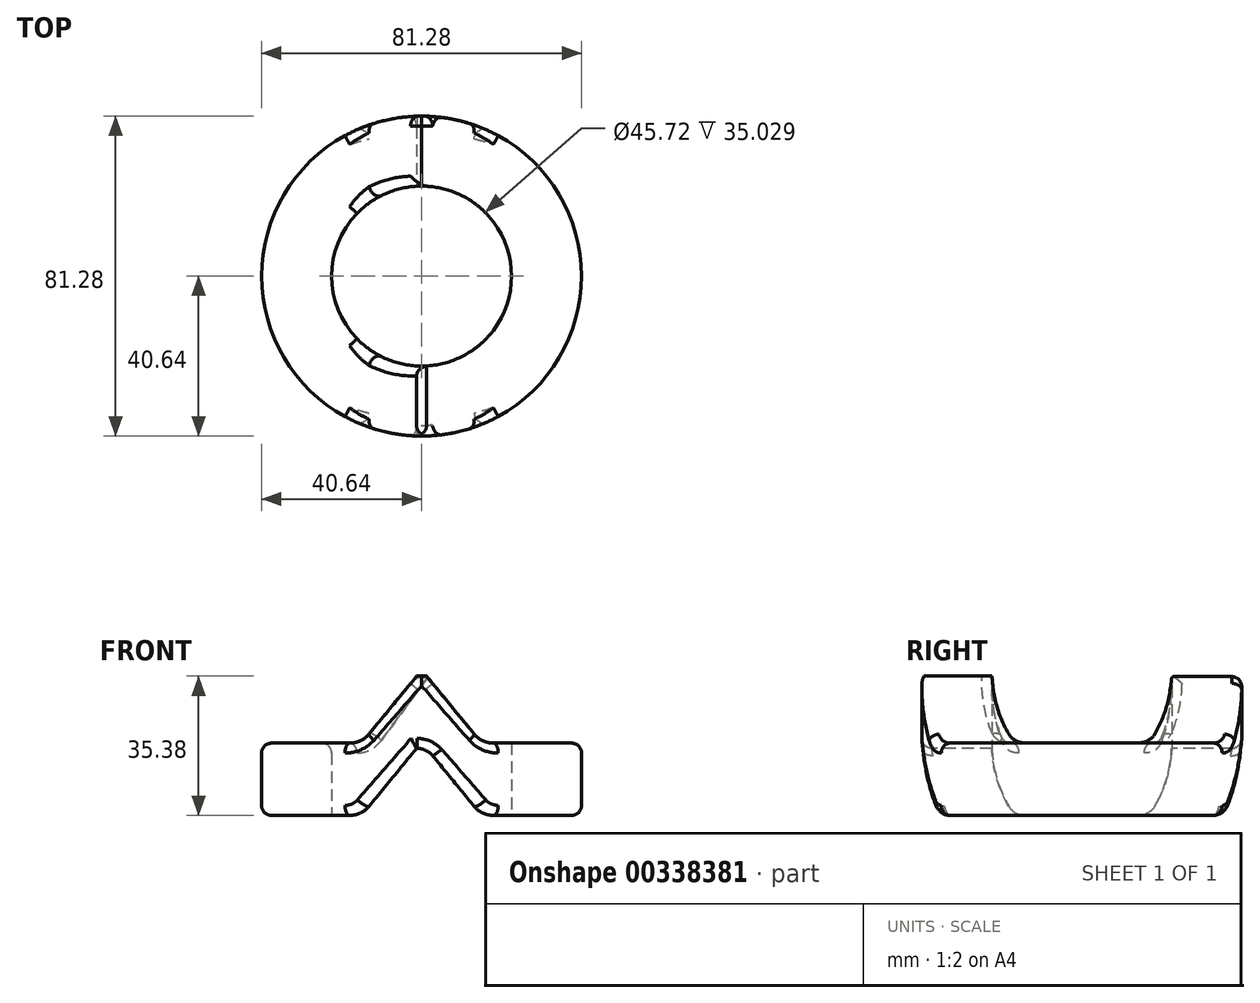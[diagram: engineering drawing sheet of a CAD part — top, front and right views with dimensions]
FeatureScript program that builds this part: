
annotation { "Feature Type Name" : "Feature", "Feature Type Description" : "" }
export const myFeature = defineFeature(function(context is Context, id is Id, definition is map)
    precondition{}
    {
        {
            var Q0;
            Q0=qCreatedBy(makeId("Top.planeOp"),FACE);
            var sketch = newSketch(context, id + "F0", { "sketchPlane" : qUnion([Q0])});
            skCircle(sketch, "E0", {"center": v(0, 0) * mm, "radius": 22.86 * mm});
            skCircle(sketch, "E1", {"center": v(0, 0) * mm, "radius": 40.64 * mm});
            skSolve(sketch);
        }
        {
            var Q0;
            Q0=makeQuery(id+"F0.imprint","IMPRINT",FACE,{"disambiguationData":[TD([[makeQuery(id+"F0.imprint","IMPRINT",EDGE,{"derivedFrom":sQuery(id+"F0.wireOp",EDGE,"E0")}),-1.0]])]});
            extrude(context, id + "F1", {"entities" : qUnion([Q0]), "depth" : 50.8 * mm});
        }
        {
            var Q0;
            Q0=qCreatedBy(makeId("Front.planeOp"),FACE);
            cPlane(context, id + "F2", {"entities" : qUnion([Q0]), "cplaneType" : CPlaneType.OFFSET, "offset" : 54.86 * mm, "width" : 152.4 * mm, "height" : 152.4 * mm});
        }
        {
            var Q0;
            Q0=qCreatedBy(id+"F2.planeOp",FACE);
            var sketch = newSketch(context, id + "F3", { "sketchPlane" : qUnion([Q0])});
            skLineSegment(sketch, "E2.top", {"start": v(-38.1, 33.78) * mm, "end": v(-18.24, 33.78) * mm});
            skLineSegment(sketch, "E2.right", {"start": v(38.1, -30.33) * mm, "end": v(38.1, -26.87) * mm});
            skPoint(sketch, "E2.middle", {"position": v(0, 0) * mm});
            skPoint(sketch, "E2.bottom.start.orphan", {"position": v(-38.1, -33.78) * mm});
            skPoint(sketch, "E3.orphan", {"position": v(38.1, -33.78) * mm});
            skLineSegment(sketch, "E4", {"start": v(0, 50.8) * mm, "end": v(0, 0) * mm});
            skLineSegment(sketch, "E5", {"start": v(-1.24, 50.8) * mm, "end": v(1.24, 50.8) * mm});
            skLineSegment(sketch, "E6", {"start": v(-1.29, 50.78) * mm, "end": v(-13.33, 36.1) * mm});
            skPoint(sketch, "E7.newPointA", {"position": v(-15.24, 33.78) * mm});
            skPoint(sketch, "E7.newPointB", {"position": v(38.1, 33.78) * mm});
            skArc(sketch, "E7.filletArc", {"start": v(-18.24, 33.78) * mm, "mid": v(-15.53, 34.4) * mm, "end": v(-13.33, 36.1) * mm});
            skPoint(sketch, "E8.visualSharp", {"position": v(15.24, 33.78) * mm});
            skPoint(sketch, "E9.visualSharp", {"position": v(1.27, 50.8) * mm});
            skPoint(sketch, "E10.visualSharp", {"position": v(-1.27, 50.8) * mm});
            skLineSegment(sketch, "E11", {"start": v(-38.1, 50.8) * mm, "end": v(-38.1, 59.33) * mm});
            skLineSegment(sketch, "E12", {"start": v(-0.13, 50.8) * mm, "end": v(-38.1, 50.8) * mm});
            skLineSegment(sketch, "E13", {"start": v(-38.1, 50.8) * mm, "end": v(38.1, 50.8) * mm});
            skLineSegment(sketch, "E14", {"start": v(-1.29, 50.78) * mm, "end": v(-1.27, 50.8) * mm});
            skLineSegment(sketch, "E15", {"start": v(1.29, 50.78) * mm, "end": v(1.27, 50.8) * mm});
            skLineSegment(sketch, "E16.MirrorCS", {"start": v(38.1, 0) * mm, "end": v(38.1, 33.78) * mm});
            skLineSegment(sketch, "E17.MirrorCS", {"start": v(38.1, 33.78) * mm, "end": v(18.24, 33.78) * mm});
            skArc(sketch, "E18.MirrorCS", {"start": v(18.24, 33.78) * mm, "mid": v(15.53, 34.4) * mm, "end": v(13.33, 36.1) * mm});
            skLineSegment(sketch, "E19.MirrorCS", {"start": v(1.29, 50.78) * mm, "end": v(13.33, 36.1) * mm});
            skPoint(sketch, "E2.left.start.orphan", {"position": v(-38.1, 0) * mm});
            skLineSegment(sketch, "E20.bottom", {"start": v(-38.1, 59.33) * mm, "end": v(-43.42, 59.33) * mm});
            skLineSegment(sketch, "E20.top", {"start": v(-38.1, 0) * mm, "end": v(-43.42, 0) * mm});
            skLineSegment(sketch, "E20.left", {"start": v(-38.1, 59.33) * mm, "end": v(-38.1, 0) * mm});
            skLineSegment(sketch, "E20.right", {"start": v(-43.42, 59.33) * mm, "end": v(-43.42, 0) * mm});
            skLineSegment(sketch, "E21.bottom", {"start": v(-38.1, 33.78) * mm, "end": v(-43.42, 33.78) * mm});
            skLineSegment(sketch, "E21.top", {"start": v(-38.1, 33.78) * mm, "end": v(-43.42, 33.78) * mm});
            skLineSegment(sketch, "E21.left", {"start": v(-38.1, 33.78) * mm, "end": v(-38.1, 33.78) * mm});
            skLineSegment(sketch, "E21.right", {"start": v(-43.42, 33.78) * mm, "end": v(-43.42, 33.78) * mm});
            skLineSegment(sketch, "E22.bottom", {"start": v(38.1, 50.8) * mm, "end": v(41.58, 50.8) * mm});
            skLineSegment(sketch, "E22.top", {"start": v(38.1, 0) * mm, "end": v(41.58, 0) * mm});
            skLineSegment(sketch, "E22.left", {"start": v(38.1, 50.8) * mm, "end": v(38.1, 0) * mm});
            skLineSegment(sketch, "E22.right", {"start": v(41.58, 50.8) * mm, "end": v(41.58, 0) * mm});
            skLineSegment(sketch, "E23.bottom", {"start": v(38.1, 33.78) * mm, "end": v(41.58, 33.78) * mm});
            skLineSegment(sketch, "E23.top", {"start": v(38.1, 33.78) * mm, "end": v(41.58, 33.78) * mm});
            skLineSegment(sketch, "E23.left", {"start": v(38.1, 33.78) * mm, "end": v(38.1, 33.78) * mm});
            skLineSegment(sketch, "E23.right", {"start": v(41.58, 33.78) * mm, "end": v(41.58, 33.78) * mm});
            skLineSegment(sketch, "E24.top", {"start": v(-38.1, 15.42) * mm, "end": v(-18.24, 15.42) * mm});
            skLineSegment(sketch, "E24.left", {"start": v(-38.1, -18.36) * mm, "end": v(-38.1, 15.42) * mm});
            skLineSegment(sketch, "E24.right", {"start": v(38.1, -18.36) * mm, "end": v(38.1, 15.42) * mm});
            skPoint(sketch, "E24.middle", {"position": v(0, -18.36) * mm});
            skLineSegment(sketch, "E25", {"start": v(-38.1, -18.36) * mm, "end": v(38.1, -18.36) * mm});
            skPoint(sketch, "E24.bottom.start.orphan", {"position": v(-38.1, -52.14) * mm});
            skPoint(sketch, "E26.orphan", {"position": v(38.1, -52.14) * mm});
            skLineSegment(sketch, "E27", {"start": v(0, 32.44) * mm, "end": v(0, -18.36) * mm});
            skLineSegment(sketch, "E28", {"start": v(-1.24, 32.44) * mm, "end": v(1.24, 32.44) * mm});
            skLineSegment(sketch, "E29", {"start": v(1.29, 32.42) * mm, "end": v(13.33, 17.74) * mm});
            skLineSegment(sketch, "E30", {"start": v(-1.29, 32.42) * mm, "end": v(-13.33, 17.74) * mm});
            skPoint(sketch, "E31.newPointA", {"position": v(-15.24, 15.42) * mm});
            skPoint(sketch, "E31.newPointB", {"position": v(38.1, 15.42) * mm});
            skArc(sketch, "E31.filletArc", {"start": v(-18.24, 15.42) * mm, "mid": v(-15.53, 16.03) * mm, "end": v(-13.33, 17.74) * mm});
            skLineSegment(sketch, "E32", {"start": v(38.1, 15.42) * mm, "end": v(18.24, 15.42) * mm});
            skPoint(sketch, "E33.visualSharp", {"position": v(15.24, 15.42) * mm});
            skArc(sketch, "E33.filletArc", {"start": v(13.33, 17.74) * mm, "mid": v(15.53, 16.03) * mm, "end": v(18.24, 15.42) * mm});
            skPoint(sketch, "E34.visualSharp", {"position": v(1.27, 32.44) * mm});
            skPoint(sketch, "E35.visualSharp", {"position": v(-1.27, 32.44) * mm});
            skLineSegment(sketch, "E36", {"start": v(-38.1, 15.42) * mm, "end": v(-38.1, 32.73) * mm});
            skLineSegment(sketch, "E37", {"start": v(38.1, 15.42) * mm, "end": v(38.1, 35.06) * mm});
            skLineSegment(sketch, "E38", {"start": v(-0.13, 32.44) * mm, "end": v(-38.1, 32.44) * mm});
            skLineSegment(sketch, "E39", {"start": v(-38.1, 32.44) * mm, "end": v(38.1, 32.44) * mm});
            skLineSegment(sketch, "E40", {"start": v(-1.29, 32.42) * mm, "end": v(-1.27, 32.44) * mm});
            skLineSegment(sketch, "E41", {"start": v(1.29, 32.42) * mm, "end": v(1.27, 32.44) * mm});
            skLineSegment(sketch, "E42", {"start": v(-38.1, 15.42) * mm, "end": v(-43.42, 15.42) * mm});
            skLineSegment(sketch, "E43", {"start": v(38.1, 15.42) * mm, "end": v(41.58, 15.42) * mm});
            skSolve(sketch);
        }
        {
            var Q0;
            {var subQ9=sQuery(id+"F3.wireOp",EDGE,"E24.top");Q0=makeQuery(id+"F3.imprint","IMPRINT",FACE,{"disambiguationData":[TD([[makeQuery(id+"F3.imprint","IMPRINT",EDGE,{"derivedFrom":subQ9}),-1.0]])]});}
            var Q1;
            {var subQ0=sQuery(id+"F3.wireOp",EDGE,"E20.top");Q1=makeQuery(id+"F3.imprint","IMPRINT",FACE,{"disambiguationData":[TD([[makeQuery(id+"F3.imprint","IMPRINT",EDGE,{"derivedFrom":subQ0}),-1.0]])]});}
            var Q2;
            Q2=makeQuery(id+"F3.imprint","IMPRINT",FACE,{"disambiguationData":[TD([[makeQuery(id+"F3.imprint","IMPRINT",EDGE,{"derivedFrom":sQuery(id+"F3.wireOp",EDGE,"E29")}),-1.0]])]});
            var Q3;
            {var subQ0=sQuery(id+"F3.wireOp",EDGE,"E22.top");Q3=makeQuery(id+"F3.imprint","IMPRINT",FACE,{"disambiguationData":[TD([[makeQuery(id+"F3.imprint","IMPRINT",EDGE,{"derivedFrom":subQ0}),1.0]])]});}
            var Q4;
            {var subQ1=sQuery(id+"F3.wireOp",EDGE,"E15");Q4=makeQuery(id+"F3.imprint","IMPRINT",FACE,{"disambiguationData":[TD([[makeQuery(id+"F3.imprint","IMPRINT",EDGE,{"derivedFrom":subQ1}),-1.0]])]});}
            var Q5;
            {var subQ2=sQuery(id+"F3.wireOp",EDGE,"E22.bottom");Q5=makeQuery(id+"F3.imprint","IMPRINT",FACE,{"disambiguationData":[TD([[makeQuery(id+"F3.imprint","IMPRINT",EDGE,{"derivedFrom":subQ2}),-1.0]])]});}
            var Q6;
            {var subQ4=sQuery(id+"F3.wireOp",EDGE,"E2.top");Q6=makeQuery(id+"F3.imprint","IMPRINT",FACE,{"disambiguationData":[TD([[makeQuery(id+"F3.imprint","IMPRINT",EDGE,{"derivedFrom":subQ4}),1.0]])]});}
            var Q7;
            {var subQ3=sQuery(id+"F3.wireOp",EDGE,"E20.bottom");Q7=makeQuery(id+"F3.imprint","IMPRINT",FACE,{"disambiguationData":[TD([[makeQuery(id+"F3.imprint","IMPRINT",EDGE,{"derivedFrom":subQ3}),1.0]])]});}
            extrude(context, id + "F4", {"entities" : qUnion([Q0, Q1, Q2, Q3, Q4, Q5, Q6, Q7]), "operationType" : NewBodyOperationType.REMOVE, "endBound" : BoundingType.THROUGH_ALL, "oppositeDirection" : true, "depth" : 25.4 * mm});
        }
        {
            var Q0;
            Q0=makeQuery(id+"F4.boolean.opBoolean","COPY",EDGE,{"disambiguationData":[OD(0.0)],"derivedFrom":makeQuery(id+"F4.opExtrude","SWEPT_EDGE",EDGE,{"disambiguationData":[OSD([sQuery(id+"F3.wireOp",EDGE,"E13"),sQuery(id+"F3.wireOp",EDGE,"E15")])]})});
            var Q1;
            Q1=makeQuery(id+"F4.boolean.opBoolean","COPY",EDGE,{"disambiguationData":[OD(1.0)],"derivedFrom":makeQuery(id+"F4.opExtrude","SWEPT_EDGE",EDGE,{"disambiguationData":[OSD([sQuery(id+"F3.wireOp",EDGE,"E13"),sQuery(id+"F3.wireOp",EDGE,"E14")])]})});
            var Q2;
            Q2=makeQuery(id+"F4.boolean.opBoolean","COPY",EDGE,{"disambiguationData":[OD(0.0)],"derivedFrom":makeQuery(id+"F4.opExtrude","SWEPT_EDGE",EDGE,{"disambiguationData":[OSD([sQuery(id+"F3.wireOp",EDGE,"E39"),sQuery(id+"F3.wireOp",EDGE,"E40")])]})});
            var Q3;
            Q3=makeQuery(id+"F4.boolean.opBoolean","COPY",EDGE,{"disambiguationData":[OD(0.0)],"derivedFrom":makeQuery(id+"F4.opExtrude","SWEPT_EDGE",EDGE,{"disambiguationData":[OSD([sQuery(id+"F3.wireOp",EDGE,"E39"),sQuery(id+"F3.wireOp",EDGE,"E41")])]})});
            var Q4;
            Q4=makeQuery(id+"F4.boolean.opBoolean","COPY",EDGE,{"disambiguationData":[OD(1.0)],"derivedFrom":makeQuery(id+"F4.opExtrude","SWEPT_EDGE",EDGE,{"disambiguationData":[OSD([sQuery(id+"F3.wireOp",EDGE,"E39"),sQuery(id+"F3.wireOp",EDGE,"E41")])]})});
            var Q5;
            Q5=makeQuery(id+"F4.boolean.opBoolean","COPY",EDGE,{"disambiguationData":[OD(1.0)],"derivedFrom":makeQuery(id+"F4.opExtrude","SWEPT_EDGE",EDGE,{"disambiguationData":[OSD([sQuery(id+"F3.wireOp",EDGE,"E39"),sQuery(id+"F3.wireOp",EDGE,"E40")])]})});
            var Q6;
            Q6=makeQuery(id+"F4.boolean.opBoolean","COPY",EDGE,{"disambiguationData":[OD(1.0)],"derivedFrom":makeQuery(id+"F4.opExtrude","SWEPT_EDGE",EDGE,{"disambiguationData":[OSD([sQuery(id+"F3.wireOp",EDGE,"E13"),sQuery(id+"F3.wireOp",EDGE,"E15")])]})});
            var Q7;
            Q7=makeQuery(id+"F4.boolean.opBoolean","COPY",EDGE,{"disambiguationData":[OD(0.0)],"derivedFrom":makeQuery(id+"F4.opExtrude","SWEPT_EDGE",EDGE,{"disambiguationData":[OSD([sQuery(id+"F3.wireOp",EDGE,"E13"),sQuery(id+"F3.wireOp",EDGE,"E14")])]})});
            fillet(context, id + "F5", {"entities" : qUnion([Q0, Q1, Q2, Q3, Q4, Q5, Q6, Q7]), "radius" : 5.08 * mm, "tangentPropagation" : true, "allowEdgeOverflow" : false});
        }
        {
            var Q0;
            Q0=makeQuery(id+"F4.boolean.opBoolean","INTERSECT",EDGE,{"derivedFrom":[makeQuery(id+"F1.opExtrude","SWEPT_FACE",FACE,{"disambiguationData":[OSD([sQuery(id+"F0.wireOp",EDGE,"E1")])]}),makeQuery(id+"F4.opExtrude","SWEPT_FACE",FACE,{"disambiguationData":[OSD([sQuery(id+"F3.wireOp",EDGE,"E17.MirrorCS"),sQuery(id+"F3.wireOp",EDGE,"E23.top")])]})]});
            var Q1;
            Q1=makeQuery(id+"F4.boolean.opBoolean","COPY",FACE,{"derivedFrom":makeQuery(id+"F4.opExtrude","SWEPT_FACE",FACE,{"disambiguationData":[OSD([sQuery(id+"F3.wireOp",EDGE,"E2.top"),sQuery(id+"F3.wireOp",EDGE,"E21.top")])]})});
            var Q2;
            Q2=makeQuery(id+"F4.boolean.opBoolean","INTERSECT",EDGE,{"derivedFrom":[makeQuery(id+"F1.opExtrude","SWEPT_FACE",FACE,{"disambiguationData":[OSD([sQuery(id+"F0.wireOp",EDGE,"E1")])]}),makeQuery(id+"F4.opExtrude","SWEPT_FACE",FACE,{"disambiguationData":[OSD([sQuery(id+"F3.wireOp",EDGE,"E24.top"),sQuery(id+"F3.wireOp",EDGE,"E42")])]})]});
            var Q3;
            Q3=makeQuery(id+"F4.boolean.opBoolean","INTERSECT",EDGE,{"derivedFrom":[makeQuery(id+"F1.opExtrude","SWEPT_FACE",FACE,{"disambiguationData":[OSD([sQuery(id+"F0.wireOp",EDGE,"E1")])]}),makeQuery(id+"F4.opExtrude","SWEPT_FACE",FACE,{"disambiguationData":[OSD([sQuery(id+"F3.wireOp",EDGE,"E32"),sQuery(id+"F3.wireOp",EDGE,"E43")])]})]});
            fillet(context, id + "F6", {"entities" : qUnion([Q0, Q1, Q2, Q3]), "radius" : 2.54 * mm, "tangentPropagation" : true, "allowEdgeOverflow" : false});
        }
    });
